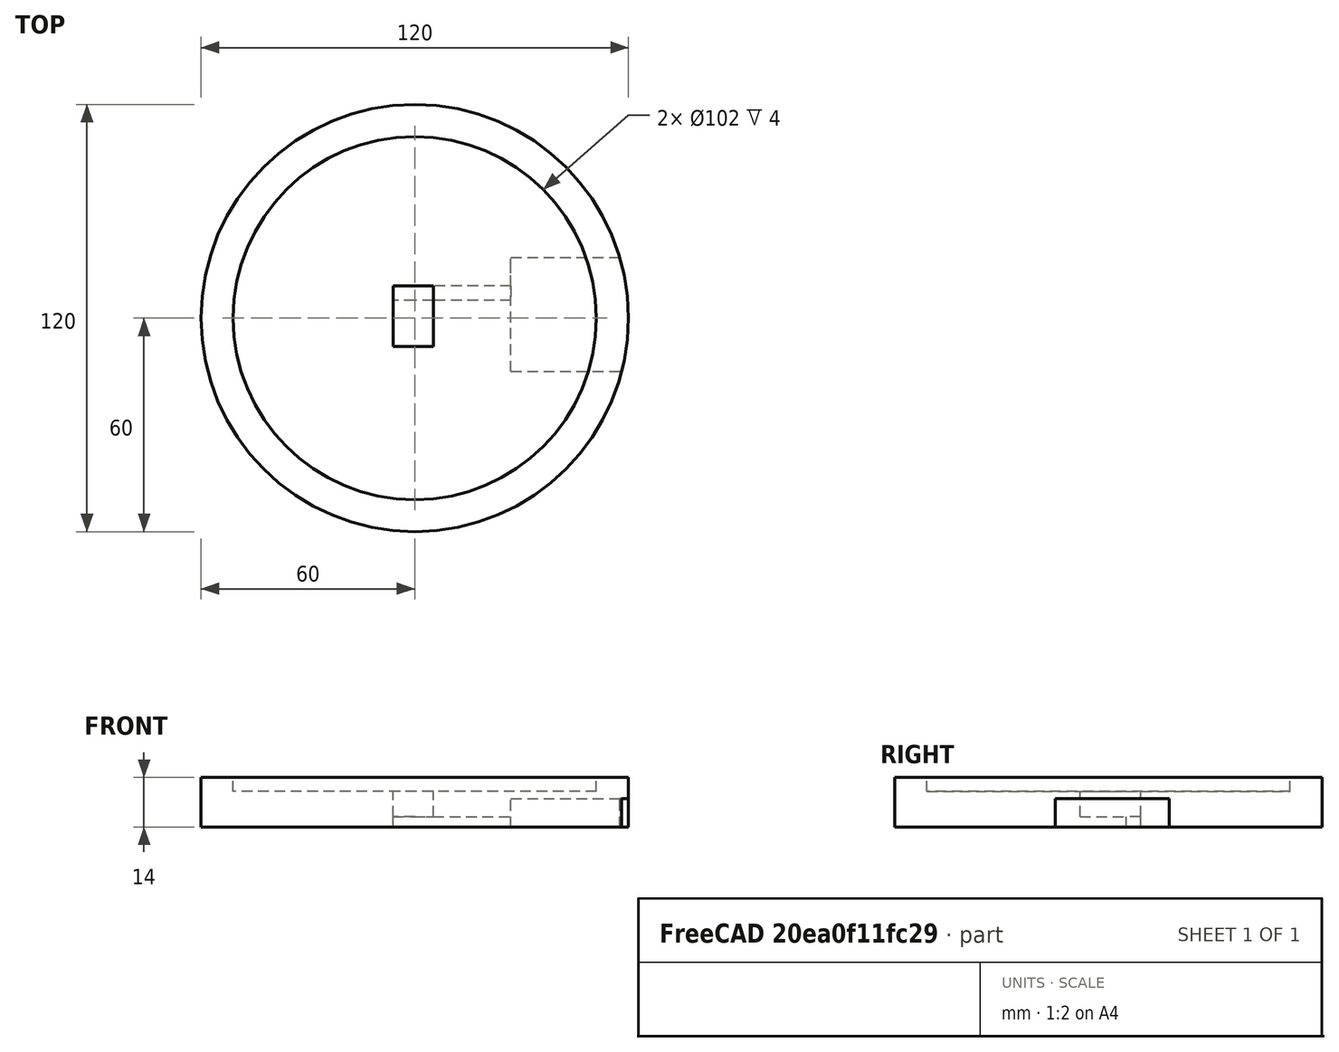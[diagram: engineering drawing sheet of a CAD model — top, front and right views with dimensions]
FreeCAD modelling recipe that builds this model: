
FCSTD DOCUMENT  (FreeCAD 0.15R4671 (Git))
Label: tealemetry
License: All rights reserved
LicenseURL: http://en.wikipedia.org/wiki/All_rights_reserved
objects: Part::Cut×6, Part::Box×4, Part::Cylinder×2
note: 12 computed .brp shape members not serialized (recipe doc carries the construction recipe); baked Part::Feature solids carry a one-line shape summary decoded from their .brp

FEATURE [Part::Cylinder] Cylinder
  Angle = 360
  Height = 5
  Placement = pos=(0,0,6) rot=(0,0,1;0rad)
  Radius = 51
FEATURE [Part::Cylinder] Cylinder001
  Angle = 360
  Height = 14
  Placement = pos=(0,0,-4) rot=(0,0,1;0rad)
  Radius = 60
FEATURE [Part::Box] Box  label="Cube"
  Height = 8
  Length = 11.2
  Placement = pos=(-6,-8,-1) rot=(0,0,1;0rad)
  Width = 17
FEATURE [Part::Cut] Cut001
  Base = -> Cylinder001
  Tool = -> Cylinder
FEATURE [Part::Cut] Cut002
  Base = -> Cut001
  Tool = -> Box
FEATURE [Part::Box] Box001  label="Cube001"
  Height = 27
  Length = 11.2
  Placement = pos=(-6,5,-18) rot=(0,0,1;0rad)
  Width = 4
FEATURE [Part::Cut] Cut003
  Base = -> Cut002
  Tool = -> Box001
FEATURE [Part::Box] Box002  label="Cube002"
  Height = 9
  Length = 34
  Placement = pos=(27,-15,-5) rot=(0,0,1;0rad)
  Width = 32
FEATURE [Part::Cut] Cut004
  Base = -> Cut003
  Tool = -> Box002
FEATURE [Part::Box] Box003  label="Cube003"
  Height = 4
  Length = 29
  Placement = pos=(0,5,-5) rot=(0,0,1;0rad)
  Width = 4
FEATURE [Part::Cut] Cut005
  Base = -> Cut004
  Tool = -> Box003
FEATURE [Part::Cut] Cut
  Base = -> Cylinder001
  Tool = -> Cylinder
